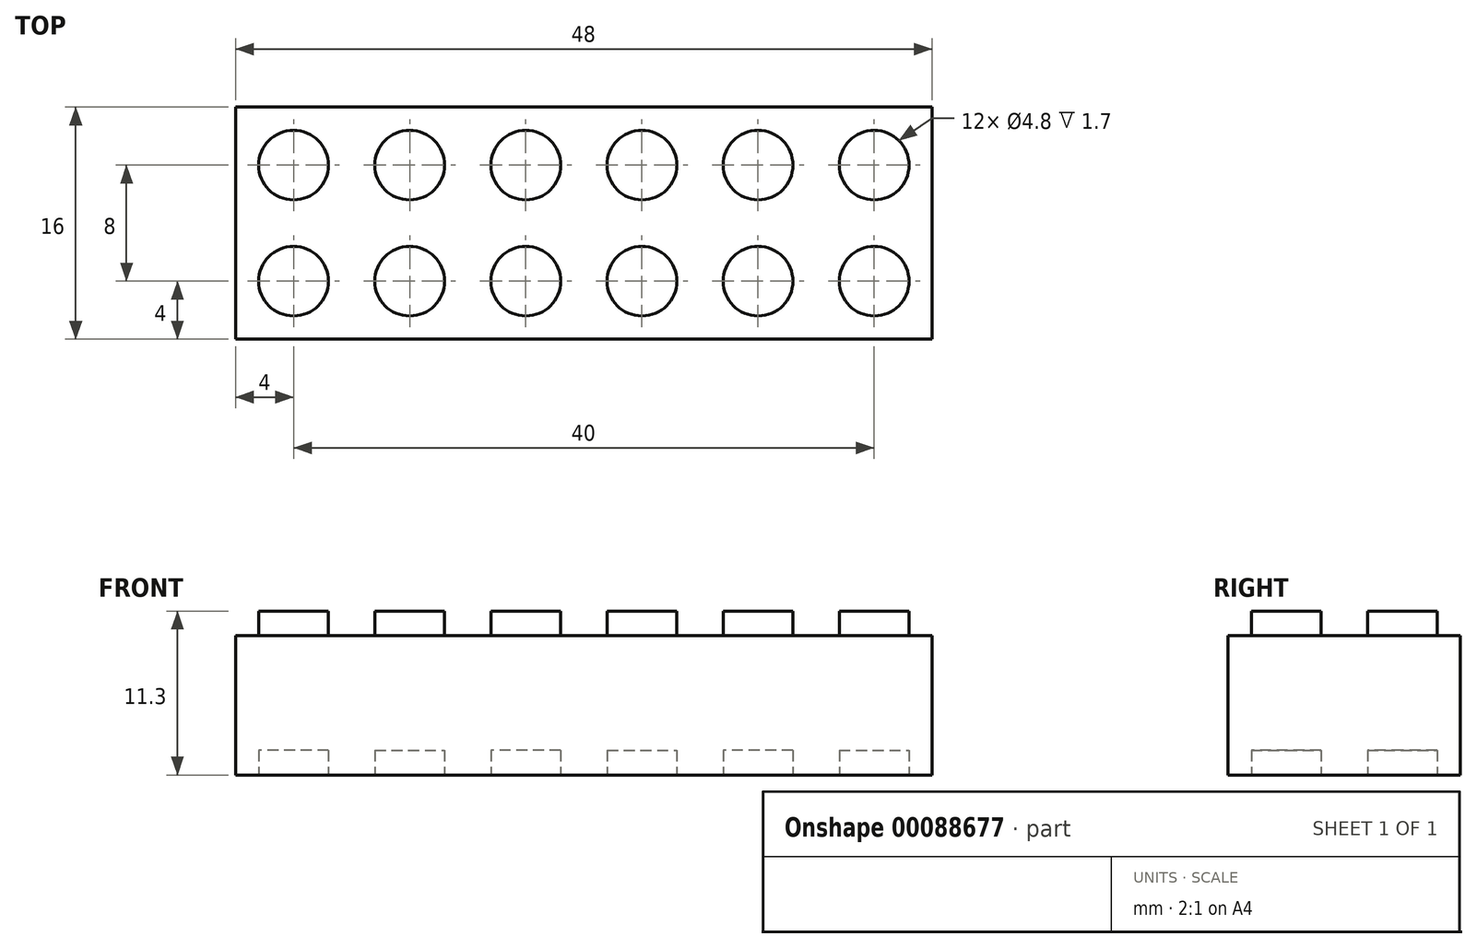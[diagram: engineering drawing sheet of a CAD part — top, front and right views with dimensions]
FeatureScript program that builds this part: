
annotation { "Feature Type Name" : "Feature", "Feature Type Description" : "" }
export const myFeature = defineFeature(function(context is Context, id is Id, definition is map)
    precondition{}
    {
        {
            var Q0;
            Q0=qCreatedBy(makeId("Front.planeOp"),FACE);
            var sketch = newSketch(context, id + "F0", { "sketchPlane" : qUnion([Q0])});
            skLineSegment(sketch, "E0.bottom", {"start": v(-4, 9.6) * mm, "end": v(-2.4, 9.6) * mm});
            skLineSegment(sketch, "E0.top", {"start": v(-4, 0) * mm, "end": v(4, 0) * mm});
            skLineSegment(sketch, "E0.left", {"start": v(-4, 9.6) * mm, "end": v(-4, 0) * mm});
            skLineSegment(sketch, "E0.right", {"start": v(4, 9.6) * mm, "end": v(4, 0) * mm});
            skLineSegment(sketch, "E1.top", {"start": v(-2.4, 11.3) * mm, "end": v(2.4, 11.3) * mm});
            skLineSegment(sketch, "E1.left", {"start": v(-2.4, 9.6) * mm, "end": v(-2.4, 11.3) * mm});
            skLineSegment(sketch, "E1.right", {"start": v(2.4, 9.6) * mm, "end": v(2.4, 11.3) * mm});
            skLineSegment(sketch, "E2", {"start": v(0, 0) * mm, "end": v(0, 24.04) * mm, "construction": true});
            skLineSegment(sketch, "E3.trimOffspring", {"start": v(2.4, 9.6) * mm, "end": v(4, 9.6) * mm});
            skSolve(sketch);
        }
        {
            var Q0;
            Q0=makeQuery(id+"F0.imprint","IMPRINT",FACE,{"disambiguationData":[TD([[makeQuery(id+"F0.imprint","IMPRINT",EDGE,{"derivedFrom":sQuery(id+"F0.wireOp",EDGE,"E0.bottom")}),-1.0]])]});
            extrude(context, id + "F1", {"entities" : qUnion([Q0]), "depth" : 8 * mm});
        }
        {
            var Q0;
            Q0=qCreatedBy(makeId("Top.planeOp"),FACE);
            var Q1;
            Q1=makeQuery(id+"F1.opExtrude","CAP_VERTEX",VERTEX,{"disambiguationData":[OSD([sQuery(id+"F0.wireOp",EDGE,"E1.top"),sQuery(id+"F0.wireOp",EDGE,"E1.right")])],"isStart":true});
            cPlane(context, id + "F2", {"entities" : qUnion([Q0, Q1]), "cplaneType" : CPlaneType.PLANE_POINT, "offset" : 152.4 * mm, "width" : 152.4 * mm, "height" : 152.4 * mm});
        }
        {
            var Q0;
            Q0=qCreatedBy(id+"F2.planeOp",FACE);
            var sketch = newSketch(context, id + "F3", { "sketchPlane" : qUnion([Q0])});
            skLineSegment(sketch, "E4.0", {"start": v(-4, -8) * mm, "end": v(-4, 0) * mm});
            skLineSegment(sketch, "E5.0", {"start": v(4, -8) * mm, "end": v(4, 0) * mm});
            skLineSegment(sketch, "E6", {"start": v(-4, 0) * mm, "end": v(4, 0) * mm});
            skLineSegment(sketch, "E7", {"start": v(-4, -8) * mm, "end": v(4, -8) * mm});
            skLineSegment(sketch, "E8", {"start": v(-4, 0) * mm, "end": v(4, -8) * mm, "construction": true});
            skLineSegment(sketch, "E9", {"start": v(-4, -8) * mm, "end": v(4, 0) * mm, "construction": true});
            skCircle(sketch, "E10", {"center": v(0, -4) * mm, "radius": 2.4 * mm});
            skSolve(sketch);
        }
        {
            var Q0;
            Q0=qSketchRegion(id+"F3",true);
            var Q1;
            Q1=makeQuery(id+"F1.opExtrude","SWEPT_FACE",FACE,{"disambiguationData":[OSD([sQuery(id+"F0.wireOp",EDGE,"E0.bottom")])]});
            extrude(context, id + "F4", {"entities" : qUnion([Q0]), "operationType" : NewBodyOperationType.REMOVE, "endBound" : BoundingType.UP_TO_SURFACE, "oppositeDirection" : true, "endBoundEntityFace" : qUnion([Q1]), "depth" : 25.4 * mm});
        }
        {
            var Q0;
            Q0=qCreatedBy(makeId("Top.planeOp"),FACE);
            var sketch = newSketch(context, id + "F5", { "sketchPlane" : qUnion([Q0])});
            skCircle(sketch, "E11.0", {"center": v(0, -4) * mm, "radius": 2.4 * mm});
            skSolve(sketch);
        }
        {
            var Q0;
            Q0=makeQuery(id+"F5.imprint","IMPRINT",FACE,{"disambiguationData":[TD([[makeQuery(id+"F5.imprint","IMPRINT",EDGE,{"derivedFrom":sQuery(id+"F5.wireOp",EDGE,"E11.0")}),1.0]])]});
            extrude(context, id + "F6", {"entities" : qUnion([Q0]), "operationType" : NewBodyOperationType.REMOVE, "depth" : 1.7 * mm});
        }
        {
            var Q0;
            Q0=qCreatedBy(makeId("Right.planeOp"),FACE);
            var Q1;
            Q1=makeQuery(id+"F1.opExtrude","CAP_VERTEX",VERTEX,{"disambiguationData":[OSD([sQuery(id+"F0.wireOp",EDGE,"E0.right"),sQuery(id+"F0.wireOp",EDGE,"E3.trimOffspring")])],"isStart":false});
            cPlane(context, id + "F7", {"entities" : qUnion([Q0, Q1]), "cplaneType" : CPlaneType.PLANE_POINT, "offset" : 152.4 * mm, "width" : 152.4 * mm, "height" : 152.4 * mm});
        }
        {
            var Q0;
            Q0=makeQuery(id+"F1.opExtrude","SWEPT_BODY",BODY,{"disambiguationData":[OSD([sQuery(id+"F0.wireOp",EDGE,"E0.bottom"),sQuery(id+"F0.wireOp",EDGE,"E0.top"),sQuery(id+"F0.wireOp",EDGE,"E0.left"),sQuery(id+"F0.wireOp",EDGE,"E0.right"),sQuery(id+"F0.wireOp",EDGE,"E1.top"),sQuery(id+"F0.wireOp",EDGE,"E1.left"),sQuery(id+"F0.wireOp",EDGE,"E1.right"),sQuery(id+"F0.wireOp",EDGE,"E3.trimOffspring")])]});
            var Q1;
            Q1=qCreatedBy(id+"F7.planeOp",FACE);
            mirror(context, id + "F8", {"operationType" : NewBodyOperationType.ADD, "entities" : qUnion([Q0]), "mirrorPlane" : qUnion([Q1])});
        }
        {
            var Q0;
            Q0=makeQuery(id+"F1.opExtrude","SWEPT_BODY",BODY,{"disambiguationData":[OSD([sQuery(id+"F0.wireOp",EDGE,"E0.bottom"),sQuery(id+"F0.wireOp",EDGE,"E0.top"),sQuery(id+"F0.wireOp",EDGE,"E0.left"),sQuery(id+"F0.wireOp",EDGE,"E0.right"),sQuery(id+"F0.wireOp",EDGE,"E1.top"),sQuery(id+"F0.wireOp",EDGE,"E1.left"),sQuery(id+"F0.wireOp",EDGE,"E1.right"),sQuery(id+"F0.wireOp",EDGE,"E3.trimOffspring")])]});
            var Q1;
            Q1=qCreatedBy(makeId("Front.planeOp"),FACE);
            mirror(context, id + "F9", {"operationType" : NewBodyOperationType.ADD, "entities" : qUnion([Q0]), "mirrorPlane" : qUnion([Q1])});
        }
        {
            var Q0;
            Q0=qCreatedBy(id+"F7.planeOp",FACE);
            var Q1;
            Q1=makeQuery(id+"F9.opPattern","COPY",VERTEX,{"derivedFrom":makeQuery(id+"F8.opPattern","COPY",VERTEX,{"derivedFrom":makeQuery(id+"F1.opExtrude","CAP_VERTEX",VERTEX,{"disambiguationData":[OSD([sQuery(id+"F0.wireOp",EDGE,"E0.bottom"),sQuery(id+"F0.wireOp",EDGE,"E0.left")])],"isStart":false}),"instanceName":"1"}),"instanceName":"1"});
            cPlane(context, id + "F10", {"entities" : qUnion([Q0, Q1]), "cplaneType" : CPlaneType.PLANE_POINT, "offset" : 152.4 * mm, "width" : 152.4 * mm, "height" : 152.4 * mm});
        }
        {
            var Q0;
            Q0=makeQuery(id+"F1.opExtrude","SWEPT_BODY",BODY,{"disambiguationData":[OSD([sQuery(id+"F0.wireOp",EDGE,"E0.bottom"),sQuery(id+"F0.wireOp",EDGE,"E0.top"),sQuery(id+"F0.wireOp",EDGE,"E0.left"),sQuery(id+"F0.wireOp",EDGE,"E0.right"),sQuery(id+"F0.wireOp",EDGE,"E1.top"),sQuery(id+"F0.wireOp",EDGE,"E1.left"),sQuery(id+"F0.wireOp",EDGE,"E1.right"),sQuery(id+"F0.wireOp",EDGE,"E3.trimOffspring")])]});
            var Q1;
            Q1=qCreatedBy(id+"F10.planeOp",FACE);
            mirror(context, id + "F11", {"operationType" : NewBodyOperationType.ADD, "entities" : qUnion([Q0]), "mirrorPlane" : qUnion([Q1])});
        }
        {
            var Q0;
            Q0=makeQuery(id+"F1.opExtrude","SWEPT_BODY",BODY,{"disambiguationData":[OSD([sQuery(id+"F0.wireOp",EDGE,"E0.bottom"),sQuery(id+"F0.wireOp",EDGE,"E0.top"),sQuery(id+"F0.wireOp",EDGE,"E0.left"),sQuery(id+"F0.wireOp",EDGE,"E0.right"),sQuery(id+"F0.wireOp",EDGE,"E1.top"),sQuery(id+"F0.wireOp",EDGE,"E1.left"),sQuery(id+"F0.wireOp",EDGE,"E1.right"),sQuery(id+"F0.wireOp",EDGE,"E3.trimOffspring")])]});
            var Q1;
            {var subQ0=makeQuery(id+"F1.opExtrude","SWEPT_FACE",FACE,{"disambiguationData":[OSD([sQuery(id+"F0.wireOp",EDGE,"E0.left")])]});Q1=makeQuery(id+"F11.opPattern","COPY",FACE,{"derivedFrom":makeQuery(id+"F9.boolean.opBoolean","MERGE",FACE,{"derivedFrom":[subQ0,makeQuery(id+"F9.opPattern","COPY",FACE,{"derivedFrom":subQ0,"instanceName":"1"})]}),"instanceName":"1"});}
            mirror(context, id + "F12", {"operationType" : NewBodyOperationType.ADD, "entities" : qUnion([Q0]), "mirrorPlane" : qUnion([Q1])});
        }
        {
            var Q0;
            {var subQ0=makeQuery(id+"F1.opExtrude","SWEPT_FACE",FACE,{"disambiguationData":[OSD([sQuery(id+"F0.wireOp",EDGE,"E0.left")])]});Q0=makeQuery(id+"F12.opPattern","COPY",FACE,{"derivedFrom":makeQuery(id+"F9.boolean.opBoolean","MERGE",FACE,{"derivedFrom":[subQ0,makeQuery(id+"F9.opPattern","COPY",FACE,{"derivedFrom":subQ0,"instanceName":"1"})]}),"instanceName":"1"});}
            cPlane(context, id + "F13", {"entities" : qUnion([Q0]), "cplaneType" : CPlaneType.OFFSET, "offset" : 0 * mm, "width" : 152.4 * mm, "height" : 152.4 * mm});
        }
        {
            var Q0;
            Q0=qCreatedBy(id+"F13.planeOp",FACE);
            var sketch = newSketch(context, id + "F14", { "sketchPlane" : qUnion([Q0])});
            skLineSegment(sketch, "E12.bottom", {"start": v(18.72, 16.7) * mm, "end": v(-14.59, 16.7) * mm});
            skLineSegment(sketch, "E12.top", {"start": v(18.72, -7.56) * mm, "end": v(-14.59, -7.56) * mm});
            skLineSegment(sketch, "E12.left", {"start": v(18.72, 16.7) * mm, "end": v(18.72, -7.56) * mm});
            skLineSegment(sketch, "E12.right", {"start": v(-14.59, 16.7) * mm, "end": v(-14.59, -7.56) * mm});
            skPoint(sketch, "E12.middle", {"position": v(2.06, 4.57) * mm});
            skSolve(sketch);
        }
        {
            var Q0;
            Q0=makeQuery(id+"F14.imprint","IMPRINT",FACE,{"disambiguationData":[TD([[makeQuery(id+"F14.imprint","IMPRINT",EDGE,{"derivedFrom":sQuery(id+"F14.wireOp",EDGE,"E12.bottom")}),1.0]])]});
            extrude(context, id + "F15", {"entities" : qUnion([Q0]), "operationType" : NewBodyOperationType.REMOVE, "oppositeDirection" : true, "depth" : 16 * mm, "offsetDistance" : 25.4 * mm});
        }
    });
